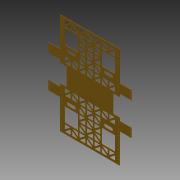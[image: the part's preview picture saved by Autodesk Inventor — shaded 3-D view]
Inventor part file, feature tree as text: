
AUTODESK INVENTOR PART (.ipt)
format: ipt  version: 2014 SP1 (Build 180222100, 222)  size: 2,093,056 bytes
history: native  units: in
note: dims shown in document units (in); Inventor stores cm internally (conversion verified against a paired STEP export)
features: sketch x7, extrude x6, hole x1, fillet x1, projected_geometry x1
ambient origin geometry x8: Origin, YZ Plane, XZ Plane, XY Plane, X Axis, Y Axis, Z Axis, Center Point
bodies: Solid1 (feature_tree)
feature tree (16):
  extrude  "Extrusion1"  Depth=20.0in
  hole  "Hole1"  [1 undecoded]
  extrude  "Extrusion2"  Depth=0.09in TaperAngle=0.0deg
  extrude  "Extrusion4"  Depth=0.5in
  extrude  "Extrusion5"  Depth=0.5in
  extrude  "Extrusion6"  Depth=0.5in
  extrude  "Extrusion7"  Depth=6.0in
  fillet  "Fillet1"  Radius=2.25in
  sketch  "Sketch1"  dims[d0=4.0in d1=20.0in]
  sketch  "Sketch2"  dims[d2=10.0in d3=3.0in]
  sketch  "Sketch4"  dims[d4=8.0in d5=0.09in d6=0.0in]
  sketch  "Sketch6"  dims[d7=0.5in d8=0.5in]
  projected_geometry  "Projected Loop2"
  sketch  "Sketch7"  dims[d9=0.5in d10=0.5in]
  sketch  "Sketch8"  dims[d11=13.3858in d13=1.0in d14=0.3937in d16=1.0in d18=0.5in]
  sketch  "Sketch9"  dims[d19=0.5in d20=0.266in d21=0.75in d22=0.375in d23=0.25in d24=0.5635in d25=1.0in d26=0.8108in d27=6.0in d28=2.25in d29=2.25in d30=6.0in d31=1.0in d32=1.0in d33=0.09in d34=0.0in d38=2.0in d96=18.0in d97=11.0in d181=2.0in d182=1.5in d184=0.5in d185=0.125in d186=0.25in d187=0.25in d188=1.5in d189=0.6875in d190=2.0in d191=1.5in d192=0.5in d193=0.125in d194=0.25in d195=0.25in d196=0.5in d197=2.0in d198=1.5in d199=0.5in d200=0.125in d201=0.25in d202=0.25in d203=2.0in d204=1.5in d205=0.5in d206=0.125in d207=0.5in d208=0.5in d209=0.5in d210=1.5in d211=2.0in d212=1.5in d213=0.5in d214=0.125in d215=0.25in d216=0.25in d217=2.0in d218=1.5in d219=0.5in d220=0.125in d221=0.25in d222=0.25in d223=0.5in d224=2.0in d225=1.5in d226=0.5in d227=0.125in d228=0.25in d229=0.25in d230=2.0in d231=1.5in d232=0.5in d233=0.125in d234=0.5in d235=0.5in d236=0.5in d237=0.5in d238=2.0in d239=1.5in d240=0.5in d241=0.125in d242=0.25in d244=2.0in d245=1.5in d246=0.5in d247=0.125in d248=0.25in d250=0.5in d251=2.0in d252=1.5in d253=0.5in d254=0.125in d255=0.25in d257=2.0in d258=1.5in d259=0.5in d260=0.125in d261=0.5in d263=0.5in d264=0.5in d265=0.6875in d266=2.0in d267=1.5in d268=0.5in d269=0.125in d270=0.25in d271=0.25in d274=2.0in d275=1.5in d276=0.5in d277=0.125in d278=0.25in d279=0.25in d280=0.5in d281=2.0in d282=1.5in d283=0.5in d284=0.125in d285=0.25in d286=0.25in d287=2.0in d288=1.5in d289=0.5in d290=0.125in d291=0.5in d292=0.5in d293=0.5in d295=2.0in d296=1.5in d297=0.5in d298=0.125in d299=0.25in d300=0.25in d301=2.0in d302=1.5in d303=0.5in d304=0.125in d305=0.25in d306=0.25in d307=0.5in d308=2.0in d309=1.5in d310=0.5in d311=0.125in d312=0.25in d313=0.25in d314=2.0in d315=1.5in d316=0.5in d317=0.125in d318=0.5in d319=0.5in d320=0.5in d321=0.5in d322=2.0in d323=1.5in d324=0.5in d325=0.125in d326=0.25in d327=2.0in d328=1.5in d329=0.5in d330=0.125in d331=0.25in d332=0.5in d333=2.0in d334=1.5in d335=0.5in d336=0.125in d337=0.25in d338=2.0in d339=1.5in d340=0.5in d341=0.125in d342=0.5in d343=0.5in d344=0.5in d346=0.6875in d347=1.0in d348=0.0in d349=0.0in d350=0.0in d351=0.0in d352=0.0in d353=0.0in d354=0.0in d355=0.0in d356=0.0in d357=0.125in d358=0.0in d359=0.0in d360=0.0in d361=0.0in d362=0.0in d363=0.0in d364=0.0in d365=0.0in d366=0.125in d367=1.0in d368=0.0in d369=0.09in d370=0.0in d371=2.0in d372=2.25in d373=1.0in d374=1.1875in d375=0.09in d376=0.0in d377=0.125in]
note: 1 required parameter value undecoded (feature->parameter linkage not recoverable at this tier; creation-order binding heuristic only, values carry confidence <= 0.55)
